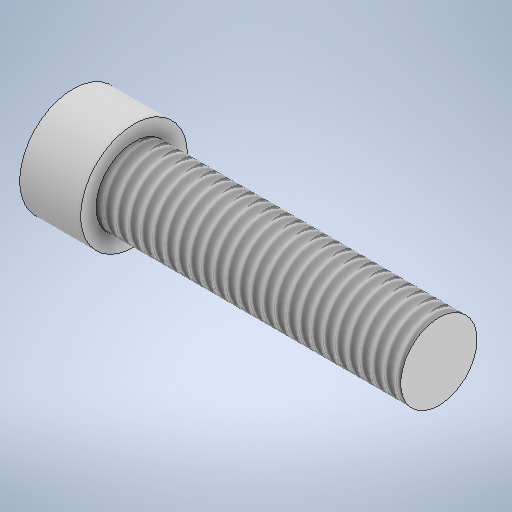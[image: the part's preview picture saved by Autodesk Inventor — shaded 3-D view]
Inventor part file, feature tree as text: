
AUTODESK INVENTOR PART (.ipt)
format: ipt  version: 2025.1 (Build 291241000, 241)  size: 295,424 bytes
history: native  units: mm
features: revolve x1, thread x1, sketch x1
ambient origin geometry x8: Origin, YZ Plane, XZ Plane, XY Plane, X Axis, Y Axis, Z Axis, Center Point
bodies: Solid1 (feature_tree)
feature tree (3):
  revolve  "Revolution1"  [1 undecoded]
  thread  "Thread1"  [1 undecoded]
  sketch  "Sketch1"  dims[d0=24.0mm d1=20.0mm d2=5.0mm d3=7.0mm d4=90.0deg d5=20.0mm d6=0.0mm]
note: 2 required parameter values undecoded (feature->parameter linkage not recoverable at this tier; creation-order binding heuristic only, values carry confidence <= 0.55)